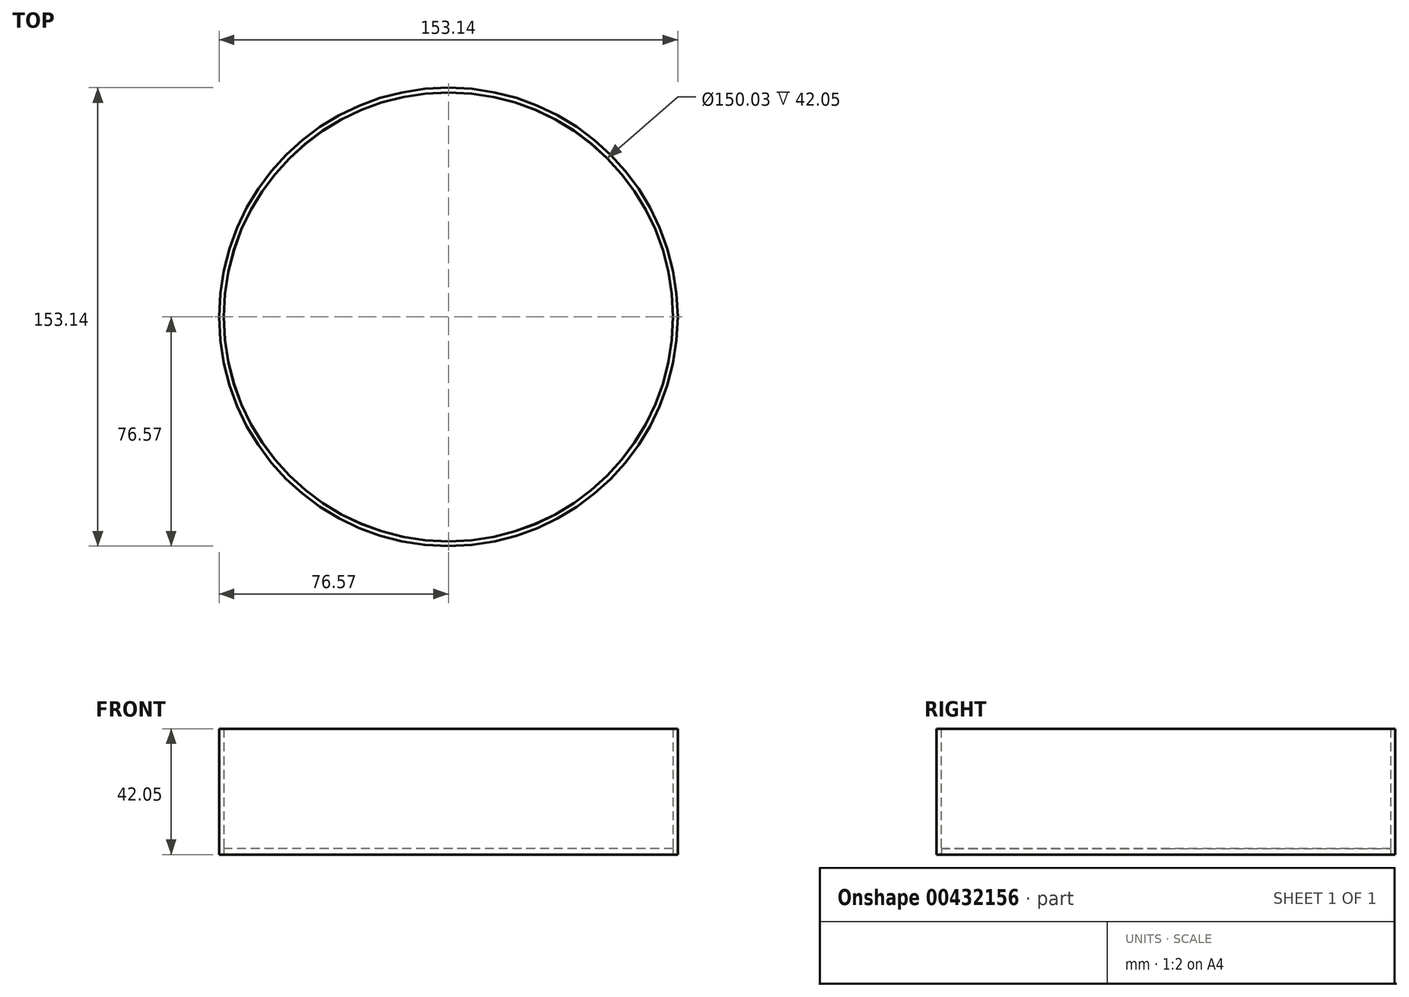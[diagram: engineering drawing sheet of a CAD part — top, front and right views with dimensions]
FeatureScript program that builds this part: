
annotation { "Feature Type Name" : "Feature", "Feature Type Description" : "" }
export const myFeature = defineFeature(function(context is Context, id is Id, definition is map)
    precondition{}
    {
        {
            var Q0;
            Q0=qCreatedBy(makeId("Top.planeOp"),FACE);
            var sketch = newSketch(context, id + "F0", { "sketchPlane" : qUnion([Q0])});
            skCircle(sketch, "E0", {"center": v(0, 0) * mm, "radius": 75 * mm});
            skSolve(sketch);
        }
        {
            var Q0;
            Q0 = qSketchRegion(id + "F0", true);
            extrude(context, id + "F1", {"entities" : qUnion([Q0]), "depth" : 2 * mm});
        }
        {
            var Q0;
            Q0=qCreatedBy(makeId("Front.planeOp"),FACE);
            var sketch = newSketch(context, id + "F2", { "sketchPlane" : qUnion([Q0])});
            skLineSegment(sketch, "E1.bottom", {"start": v(75.01, 0) * mm, "end": v(76.57, 0) * mm});
            skLineSegment(sketch, "E1.top", {"start": v(75.01, 42.05) * mm, "end": v(76.57, 42.05) * mm});
            skLineSegment(sketch, "E1.left", {"start": v(76.57, 0) * mm, "end": v(76.57, 42.05) * mm});
            skLineSegment(sketch, "E1.right", {"start": v(75.01, 0) * mm, "end": v(75.01, 42.05) * mm});
            skSolve(sketch);
        }
        {
            var Q0;
            Q0=makeQuery(id+"F2.imprint","IMPRINT",FACE,{"disambiguationData":[TD([[makeQuery(id+"F2.imprint","IMPRINT",EDGE,{"derivedFrom":sQuery(id+"F2.wireOp",EDGE,"2OkeLaxK-HJsI-Gino-r5Z9-Xx99Yl6aXUSa.bottom")}),1.0]])]});
            var Q1;
            Q1=makeQuery(id+"F2.imprint","IMPRINT",FACE,{"disambiguationData":[TD([[makeQuery(id+"F2.imprint","IMPRINT",EDGE,{"derivedFrom":sQuery(id+"F2.wireOp",EDGE,"E1.bottom")}),1.0]])]});
            var Q2;
            Q2=makeQuery(id+"F1.opExtrude","CAP_EDGE",EDGE,{"disambiguationData":[OSD([sQuery(id+"F0.wireOp",EDGE,"E0")])],"isStart":false});
            revolve(context, id + "F3", {"entities" : qUnion([Q0, Q1]), "axis" : qUnion([Q2]), "revolveType" : RevolveType.FULL});
        }
    });
